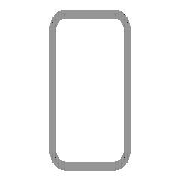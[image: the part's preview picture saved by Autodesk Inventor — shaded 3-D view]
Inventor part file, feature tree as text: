
AUTODESK INVENTOR PART (.ipt)
format: ipt  version: 2022.1 (Build 261234000, 234)  size: 137,728 bytes
history: native  units: mm (DEFAULTED — no unit token found)
features: other x3, sketch x3, extrude x1, plane x1
ambient origin geometry x8: Origin, YZ Plane, XZ Plane, XY Plane, X Axis, Y Axis, Z Axis, Center Point
bodies: Solid1 (feature_tree)
feature tree (8):
  other  "Driven Length"
  other  "Plano inicial"
  other  "Plano final"
  extrude  "Cuerpo"  Depth=20.0mm
  sketch  "Boceto1"  dims[d4=0.0mm d8=20.0mm]
  sketch  "Sketch2"  dims[d9=30.0mm]
  plane  "Work Plane3"
  sketch  "Sketch3"  dims[d10=2.9mm d11=-0.0mm d12=1400.0mm d13=90.0deg d14=1400.0mm]
